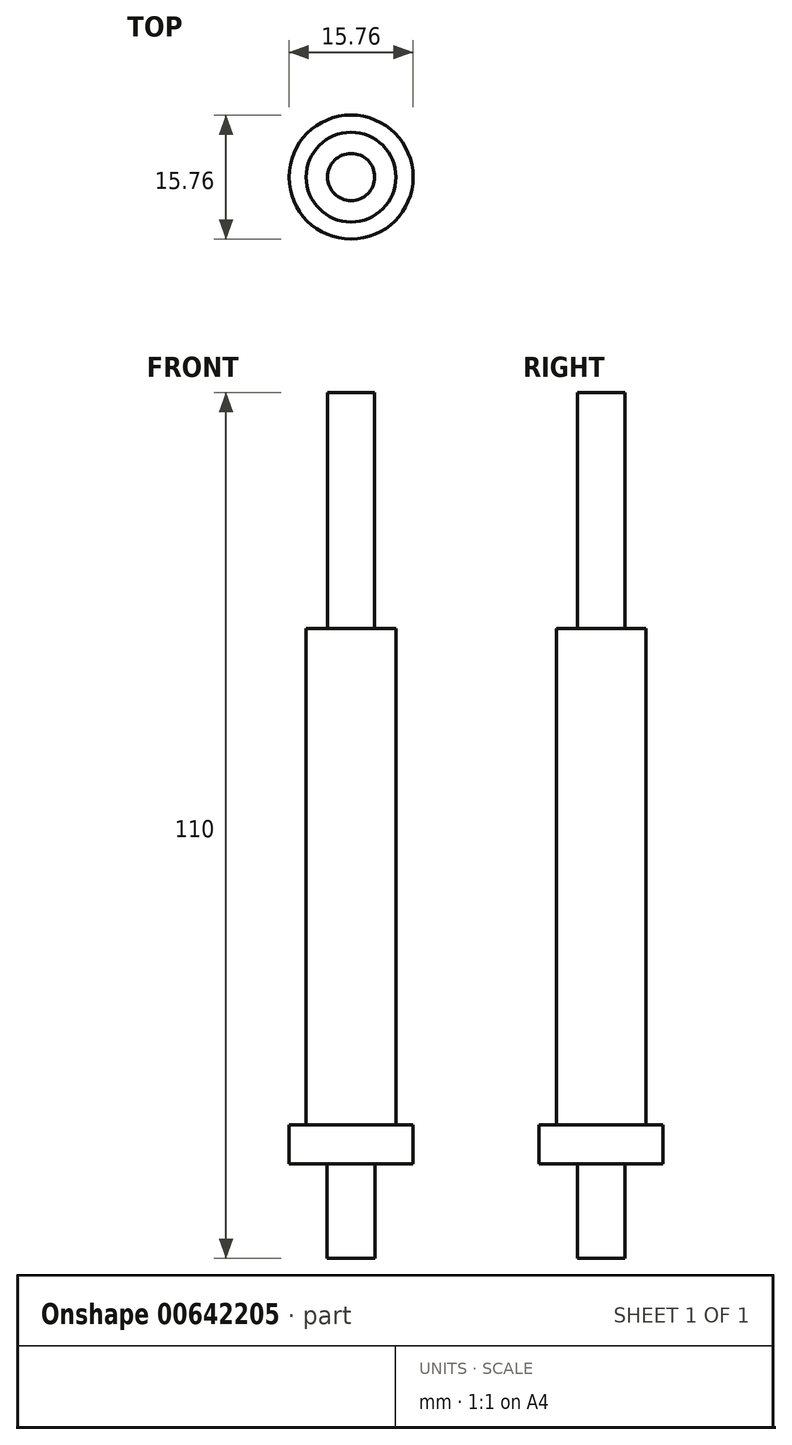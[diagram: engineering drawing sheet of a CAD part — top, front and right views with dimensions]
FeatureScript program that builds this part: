
annotation { "Feature Type Name" : "Feature", "Feature Type Description" : "" }
export const myFeature = defineFeature(function(context is Context, id is Id, definition is map)
    precondition{}
    {
        {
            var Q0;
            Q0=qCreatedBy(makeId("Top.planeOp"),FACE);
            var sketch = newSketch(context, id + "F0", { "sketchPlane" : qUnion([Q0])});
            skCircle(sketch, "E0", {"center": v(0, 0) * mm, "radius": 5.7 * mm});
            skSolve(sketch);
        }
        {
            var Q0;
            Q0 = qSketchRegion(id + "F0", true);
            extrude(context, id + "F1", {"entities" : qUnion([Q0]), "depth" : 63 * mm, "offsetDistance" : 25 * mm});
        }
        {
            var Q0;
            Q0=makeQuery(id+"F1.opExtrude","CAP_FACE",FACE,{"disambiguationData":[OSD([sQuery(id+"F0.wireOp",EDGE,"E0")])],"isStart":false});
            var sketch = newSketch(context, id + "F2", { "sketchPlane" : qUnion([Q0])});
            skCircle(sketch, "E1", {"center": v(0, 0) * mm, "radius": 3 * mm});
            skSolve(sketch);
        }
        {
            var Q0;
            Q0 = qSketchRegion(id + "F2", true);
            extrude(context, id + "F3", {"entities" : qUnion([Q0]), "operationType" : NewBodyOperationType.ADD, "depth" : 30 * mm, "offsetDistance" : 25 * mm});
        }
        {
            var Q0;
            Q0=makeQuery(id+"F1.opExtrude","CAP_FACE",FACE,{"disambiguationData":[OSD([sQuery(id+"F0.wireOp",EDGE,"E0")])],"isStart":true});
            var sketch = newSketch(context, id + "F4", { "sketchPlane" : qUnion([Q0])});
            skCircle(sketch, "E2", {"center": v(0, 0) * mm, "radius": 7.88 * mm});
            skSolve(sketch);
        }
        {
            var Q0;
            Q0 = qSketchRegion(id + "F4", true);
            extrude(context, id + "F5", {"entities" : qUnion([Q0]), "depth" : 5 * mm, "offsetDistance" : 25 * mm});
        }
        {
            var Q0;
            Q0=makeQuery(id+"F5.opExtrude","CAP_FACE",FACE,{"disambiguationData":[OSD([sQuery(id+"F4.wireOp",EDGE,"E2")])],"isStart":false});
            var sketch = newSketch(context, id + "F6", { "sketchPlane" : qUnion([Q0])});
            skCircle(sketch, "E3", {"center": v(0, 0) * mm, "radius": 3.03 * mm});
            skSolve(sketch);
        }
        {
            var Q0;
            Q0 = qSketchRegion(id + "F6", true);
            extrude(context, id + "F7", {"entities" : qUnion([Q0]), "operationType" : NewBodyOperationType.ADD, "depth" : 12 * mm, "offsetDistance" : 25 * mm});
        }
    });
